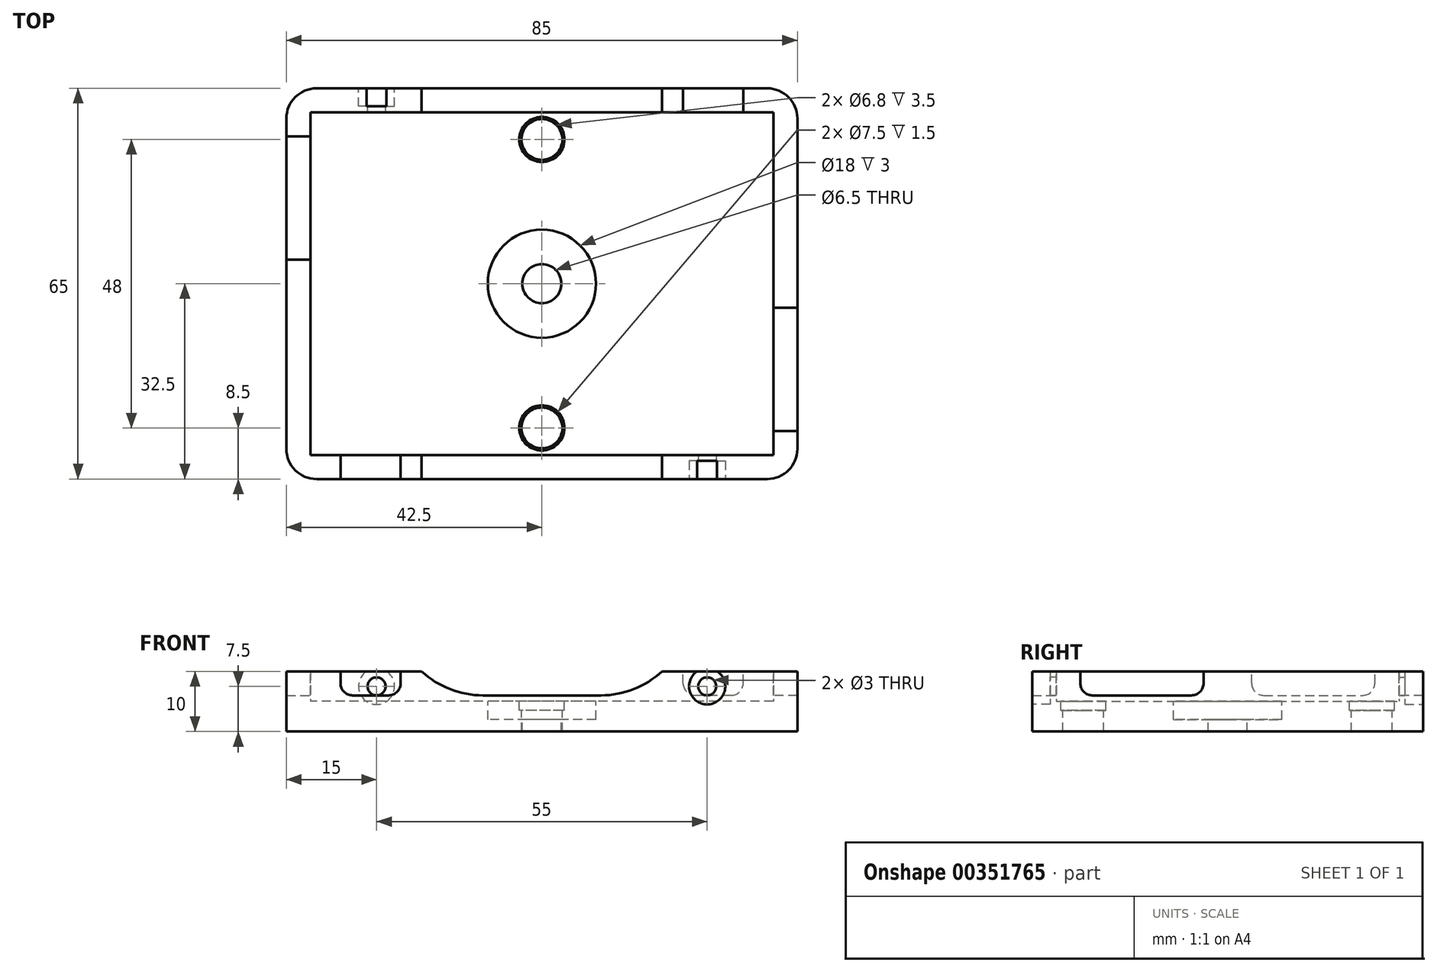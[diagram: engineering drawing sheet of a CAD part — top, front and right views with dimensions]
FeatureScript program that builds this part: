
annotation { "Feature Type Name" : "Feature", "Feature Type Description" : "" }
export const myFeature = defineFeature(function(context is Context, id is Id, definition is map)
    precondition{}
    {
        {
            var Q0;
            Q0=qCreatedBy(makeId("Top.planeOp"),FACE);
            var sketch = newSketch(context, id + "F0", { "sketchPlane" : qUnion([Q0])});
            skLineSegment(sketch, "E0.bottom", {"start": v(38.5, -28.5) * mm, "end": v(-38.5, -28.5) * mm});
            skLineSegment(sketch, "E0.top", {"start": v(38.5, 28.5) * mm, "end": v(-38.5, 28.5) * mm});
            skLineSegment(sketch, "E0.left", {"start": v(38.5, -28.5) * mm, "end": v(38.5, 28.5) * mm});
            skLineSegment(sketch, "E0.right", {"start": v(-38.5, -28.5) * mm, "end": v(-38.5, 28.5) * mm});
            skPoint(sketch, "E0.middle", {"position": v(0, 0) * mm});
            skLineSegment(sketch, "E1.0", {"start": v(42.5, 32.5) * mm, "end": v(-42.5, 32.5) * mm});
            skLineSegment(sketch, "E1.1", {"start": v(42.5, -32.5) * mm, "end": v(42.5, 32.5) * mm});
            skLineSegment(sketch, "E1.2", {"start": v(42.5, -32.5) * mm, "end": v(-42.5, -32.5) * mm});
            skLineSegment(sketch, "E1.3", {"start": v(-42.5, -32.5) * mm, "end": v(-42.5, 32.5) * mm});
            skSolve(sketch);
        }
        {
            var Q0;
            Q0=makeQuery(id+"F0.imprint","IMPRINT",FACE,{"disambiguationData":[TD([[makeQuery(id+"F0.imprint","IMPRINT",EDGE,{"derivedFrom":sQuery(id+"F0.wireOp",EDGE,"E0.bottom")}),-1.0]])]});
            var Q1;
            Q1=makeQuery(id+"F0.imprint","IMPRINT",FACE,{"disambiguationData":[TD([[makeQuery(id+"F0.imprint","IMPRINT",EDGE,{"derivedFrom":sQuery(id+"F0.wireOp",EDGE,"E0.bottom")}),1.0]])]});
            extrude(context, id + "F1", {"entities" : qUnion([Q0, Q1]), "oppositeDirection" : true, "depth" : 5 * mm, "offsetDistance" : 25 * mm});
        }
        {
            var Q0;
            Q0=makeQuery(id+"F0.imprint","IMPRINT",FACE,{"disambiguationData":[TD([[makeQuery(id+"F0.imprint","IMPRINT",EDGE,{"derivedFrom":sQuery(id+"F0.wireOp",EDGE,"E0.bottom")}),1.0]])]});
            extrude(context, id + "F2", {"entities" : qUnion([Q0]), "operationType" : NewBodyOperationType.ADD, "depth" : 5 * mm, "offsetDistance" : 25 * mm});
        }
        {
            var Q0;
            Q0=makeQuery(id+"F2.opExtrude","CAP_FACE",FACE,{"disambiguationData":[OSD([sQuery(id+"F0.wireOp",EDGE,"E0.bottom"),sQuery(id+"F0.wireOp",EDGE,"E0.top"),sQuery(id+"F0.wireOp",EDGE,"E0.left"),sQuery(id+"F0.wireOp",EDGE,"E0.right"),sQuery(id+"F0.wireOp",EDGE,"E1.0"),sQuery(id+"F0.wireOp",EDGE,"E1.1"),sQuery(id+"F0.wireOp",EDGE,"E1.2"),sQuery(id+"F0.wireOp",EDGE,"E1.3")])],"isStart":false});
            var sketch = newSketch(context, id + "F3", { "sketchPlane" : qUnion([Q0])});
            skLineSegment(sketch, "E2.bottom", {"start": v(20, 28.5) * mm, "end": v(-20, 28.5) * mm});
            skLineSegment(sketch, "E2.top", {"start": v(20, 32.5) * mm, "end": v(-20, 32.5) * mm});
            skLineSegment(sketch, "E2.left", {"start": v(20, 28.5) * mm, "end": v(20, 32.5) * mm});
            skLineSegment(sketch, "E2.right", {"start": v(-20, 28.5) * mm, "end": v(-20, 32.5) * mm});
            skPoint(sketch, "E2.middle", {"position": v(0, 30.5) * mm});
            skPoint(sketch, "E2.middle.positionSnap0", {"position": v(0, 32.5) * mm});
            skPoint(sketch, "E2.centerSnap0", {"position": v(0, 32.5) * mm});
            skLineSegment(sketch, "E3.bottom", {"start": v(20, -32.5) * mm, "end": v(-20, -32.5) * mm});
            skLineSegment(sketch, "E3.top", {"start": v(20, -28.5) * mm, "end": v(-20, -28.5) * mm});
            skLineSegment(sketch, "E3.left", {"start": v(20, -32.5) * mm, "end": v(20, -28.5) * mm});
            skLineSegment(sketch, "E3.right", {"start": v(-20, -32.5) * mm, "end": v(-20, -28.5) * mm});
            skPoint(sketch, "E3.middle", {"position": v(0, -30.5) * mm});
            skPoint(sketch, "E3.middle.positionSnap0", {"position": v(0, -32.5) * mm});
            skPoint(sketch, "E3.centerSnap0", {"position": v(0, -32.5) * mm});
            skLineSegment(sketch, "E4.bottom", {"start": v(-23.5, -28.5) * mm, "end": v(-33.5, -28.5) * mm});
            skLineSegment(sketch, "E4.top", {"start": v(-23.5, -32.5) * mm, "end": v(-33.5, -32.5) * mm});
            skLineSegment(sketch, "E4.left", {"start": v(-23.5, -28.5) * mm, "end": v(-23.5, -32.5) * mm});
            skLineSegment(sketch, "E4.right", {"start": v(-33.5, -28.5) * mm, "end": v(-33.5, -32.5) * mm});
            skPoint(sketch, "E4.middle", {"position": v(-28.5, -30.5) * mm});
            skLineSegment(sketch, "E5.bottom", {"start": v(33.5, 32.5) * mm, "end": v(23.5, 32.5) * mm});
            skLineSegment(sketch, "E5.top", {"start": v(33.5, 28.5) * mm, "end": v(23.5, 28.5) * mm});
            skLineSegment(sketch, "E5.left", {"start": v(33.5, 32.5) * mm, "end": v(33.5, 28.5) * mm});
            skLineSegment(sketch, "E5.right", {"start": v(23.5, 32.5) * mm, "end": v(23.5, 28.5) * mm});
            skPoint(sketch, "E5.middle", {"position": v(28.5, 30.5) * mm});
            skLineSegment(sketch, "E6.bottom", {"start": v(-42.5, 24.5) * mm, "end": v(-38.5, 24.5) * mm});
            skLineSegment(sketch, "E6.top", {"start": v(-42.5, 4) * mm, "end": v(-38.5, 4) * mm});
            skLineSegment(sketch, "E6.left", {"start": v(-42.5, 24.5) * mm, "end": v(-42.5, 4) * mm});
            skLineSegment(sketch, "E6.right", {"start": v(-38.5, 24.5) * mm, "end": v(-38.5, 4) * mm});
            skLineSegment(sketch, "E7.bottom", {"start": v(42.5, -24.5) * mm, "end": v(38.5, -24.5) * mm});
            skLineSegment(sketch, "E7.top", {"start": v(42.5, -4) * mm, "end": v(38.5, -4) * mm});
            skLineSegment(sketch, "E7.left", {"start": v(42.5, -24.5) * mm, "end": v(42.5, -4) * mm});
            skLineSegment(sketch, "E7.right", {"start": v(38.5, -24.5) * mm, "end": v(38.5, -4) * mm});
            skSolve(sketch);
        }
        {
            var Q0;
            Q0=makeQuery(id+"F3.imprint","IMPRINT",FACE,{"disambiguationData":[TD([[makeQuery(id+"F3.imprint","IMPRINT",EDGE,{"derivedFrom":sQuery(id+"F3.wireOp",EDGE,"E5.bottom")}),1.0]])]});
            var Q1;
            Q1=makeQuery(id+"F3.imprint","IMPRINT",FACE,{"disambiguationData":[TD([[makeQuery(id+"F3.imprint","IMPRINT",EDGE,{"derivedFrom":sQuery(id+"F3.wireOp",EDGE,"E2.bottom")}),-1.0]])]});
            var Q2;
            Q2=makeQuery(id+"F3.imprint","IMPRINT",FACE,{"disambiguationData":[TD([[makeQuery(id+"F3.imprint","IMPRINT",EDGE,{"derivedFrom":sQuery(id+"F3.wireOp",EDGE,"E3.bottom")}),-1.0]])]});
            var Q3;
            Q3=makeQuery(id+"F3.imprint","IMPRINT",FACE,{"disambiguationData":[TD([[makeQuery(id+"F3.imprint","IMPRINT",EDGE,{"derivedFrom":sQuery(id+"F3.wireOp",EDGE,"E4.bottom")}),1.0]])]});
            var Q4;
            Q4=makeQuery(id+"F3.imprint","IMPRINT",FACE,{"disambiguationData":[TD([[makeQuery(id+"F3.imprint","IMPRINT",EDGE,{"derivedFrom":sQuery(id+"F3.wireOp",EDGE,"E6.bottom")}),-1.0]])]});
            var Q5;
            Q5=makeQuery(id+"F3.imprint","IMPRINT",FACE,{"disambiguationData":[TD([[makeQuery(id+"F3.imprint","IMPRINT",EDGE,{"derivedFrom":sQuery(id+"F3.wireOp",EDGE,"E7.bottom")}),-1.0]])]});
            extrude(context, id + "F4", {"entities" : qUnion([Q0, Q1, Q2, Q3, Q4, Q5]), "operationType" : NewBodyOperationType.REMOVE, "oppositeDirection" : true, "depth" : 4 * mm, "offsetDistance" : 25 * mm});
        }
        {
            var Q0;
            Q0=makeQuery(id+"F4.boolean.opBoolean","COPY",EDGE,{"derivedFrom":makeQuery(id+"F4.opExtrude","CAP_EDGE",EDGE,{"disambiguationData":[OSD([sQuery(id+"F3.wireOp",EDGE,"E2.right")])],"isStart":false})});
            var Q1;
            Q1=makeQuery(id+"F4.boolean.opBoolean","COPY",EDGE,{"derivedFrom":makeQuery(id+"F4.opExtrude","CAP_EDGE",EDGE,{"disambiguationData":[OSD([sQuery(id+"F3.wireOp",EDGE,"E2.left")])],"isStart":false})});
            var Q2;
            Q2=makeQuery(id+"F4.boolean.opBoolean","COPY",EDGE,{"derivedFrom":makeQuery(id+"F4.opExtrude","CAP_EDGE",EDGE,{"disambiguationData":[OSD([sQuery(id+"F3.wireOp",EDGE,"E3.left")])],"isStart":false})});
            var Q3;
            Q3=makeQuery(id+"F4.boolean.opBoolean","COPY",EDGE,{"derivedFrom":makeQuery(id+"F4.opExtrude","CAP_EDGE",EDGE,{"disambiguationData":[OSD([sQuery(id+"F3.wireOp",EDGE,"E3.right")])],"isStart":false})});
            fillet(context, id + "F5", {"entities" : qUnion([Q0, Q1, Q2, Q3]), "radius" : 15 * mm, "tangentPropagation" : true, "allowEdgeOverflow" : false});
        }
        {
            var Q0;
            Q0=makeQuery(id+"F4.boolean.opBoolean","COPY",EDGE,{"derivedFrom":makeQuery(id+"F4.opExtrude","CAP_EDGE",EDGE,{"disambiguationData":[OSD([sQuery(id+"F3.wireOp",EDGE,"E7.top")])],"isStart":false})});
            var Q1;
            Q1=makeQuery(id+"F4.boolean.opBoolean","COPY",EDGE,{"derivedFrom":makeQuery(id+"F4.opExtrude","CAP_EDGE",EDGE,{"disambiguationData":[OSD([sQuery(id+"F3.wireOp",EDGE,"E7.bottom")])],"isStart":false})});
            var Q2;
            Q2=makeQuery(id+"F4.boolean.opBoolean","COPY",EDGE,{"derivedFrom":makeQuery(id+"F4.opExtrude","CAP_EDGE",EDGE,{"disambiguationData":[OSD([sQuery(id+"F3.wireOp",EDGE,"E6.bottom")])],"isStart":false})});
            var Q3;
            Q3=makeQuery(id+"F4.boolean.opBoolean","COPY",EDGE,{"derivedFrom":makeQuery(id+"F4.opExtrude","CAP_EDGE",EDGE,{"disambiguationData":[OSD([sQuery(id+"F3.wireOp",EDGE,"E6.top")])],"isStart":false})});
            var Q4;
            Q4=makeQuery(id+"F4.boolean.opBoolean","COPY",EDGE,{"derivedFrom":makeQuery(id+"F4.opExtrude","CAP_EDGE",EDGE,{"disambiguationData":[OSD([sQuery(id+"F3.wireOp",EDGE,"E4.right")])],"isStart":false})});
            var Q5;
            Q5=makeQuery(id+"F4.boolean.opBoolean","COPY",EDGE,{"derivedFrom":makeQuery(id+"F4.opExtrude","CAP_EDGE",EDGE,{"disambiguationData":[OSD([sQuery(id+"F3.wireOp",EDGE,"E4.left")])],"isStart":false})});
            var Q6;
            Q6=makeQuery(id+"F4.boolean.opBoolean","COPY",EDGE,{"derivedFrom":makeQuery(id+"F4.opExtrude","CAP_EDGE",EDGE,{"disambiguationData":[OSD([sQuery(id+"F3.wireOp",EDGE,"E5.left")])],"isStart":false})});
            var Q7;
            Q7=makeQuery(id+"F4.boolean.opBoolean","COPY",EDGE,{"derivedFrom":makeQuery(id+"F4.opExtrude","CAP_EDGE",EDGE,{"disambiguationData":[OSD([sQuery(id+"F3.wireOp",EDGE,"E5.right")])],"isStart":false})});
            fillet(context, id + "F6", {"entities" : qUnion([Q0, Q1, Q2, Q3, Q4, Q5, Q6, Q7]), "radius" : 2 * mm, "tangentPropagation" : true, "allowEdgeOverflow" : false});
        }
        {
            var Q0;
            Q0=makeQuery(id+"F0.imprint","IMPRINT",FACE,{"disambiguationData":[TD([[makeQuery(id+"F0.imprint","IMPRINT",EDGE,{"derivedFrom":sQuery(id+"F0.wireOp",EDGE,"E0.bottom")}),-1.0]])]});
            var sketch = newSketch(context, id + "F7", { "sketchPlane" : qUnion([Q0])});
            skCircle(sketch, "E8", {"center": v(0, 24) * mm, "radius": 3.25 * mm});
            skCircle(sketch, "E9", {"center": v(0, -24) * mm, "radius": 3.25 * mm});
            skSolve(sketch);
        }
        {
            var Q0;
            Q0=sQuery(id+"F7.wireOp",VERTEX,"E8.center");
            var Q1;
            Q1=sQuery(id+"F7.wireOp",VERTEX,"E9.center");
            var Q2;
            Q2=makeQuery(id+"F1.opExtrude","SWEPT_BODY",BODY,{"disambiguationData":[OSD([sQuery(id+"F0.wireOp",EDGE,"E1.0"),sQuery(id+"F0.wireOp",EDGE,"E1.1"),sQuery(id+"F0.wireOp",EDGE,"E1.2"),sQuery(id+"F0.wireOp",EDGE,"E1.3")])]});
            hole(context, id + "F8", {"style" : HoleStyle.C_BORE, "endStyle" : HoleEndStyle.THROUGH, "holeDiameter" : 6.8 * mm, "cBoreDiameter" : 7.5 * mm, "cBoreDepth" : 1.5 * mm, "majorDiameter" : 5 * mm, "isTappedThrough" : true, "tappedDepth" : 12 * mm, "tapClearance" : 3, "locations" : qUnion([Q0, Q1]), "scope" : qUnion([Q2])});
        }
        {
            var Q0;
            Q0=makeQuery(id+"F0.imprint","IMPRINT",FACE,{"disambiguationData":[TD([[makeQuery(id+"F0.imprint","IMPRINT",EDGE,{"derivedFrom":sQuery(id+"F0.wireOp",EDGE,"E0.bottom")}),-1.0]])]});
            var sketch = newSketch(context, id + "F9", { "sketchPlane" : qUnion([Q0])});
            skCircle(sketch, "E10", {"center": v(0, 0) * mm, "radius": 9 * mm});
            skCircle(sketch, "E11", {"center": v(0, 0) * mm, "radius": 3.25 * mm});
            skSolve(sketch);
        }
        {
            var Q0;
            Q0 = qSketchRegion(id + "F9", true);
            extrude(context, id + "F10", {"entities" : qUnion([Q0]), "operationType" : NewBodyOperationType.REMOVE, "oppositeDirection" : true, "depth" : 3 * mm, "offsetDistance" : 25 * mm});
        }
        {
            var Q0;
            Q0=makeQuery(id+"F9.imprint","IMPRINT",FACE,{"disambiguationData":[TD([[makeQuery(id+"F9.imprint","IMPRINT",EDGE,{"derivedFrom":sQuery(id+"F9.wireOp",EDGE,"E11")}),1.0]])]});
            extrude(context, id + "F11", {"entities" : qUnion([Q0]), "operationType" : NewBodyOperationType.REMOVE, "oppositeDirection" : true, "depth" : 25 * mm, "offsetDistance" : 25 * mm});
        }
        {
            var Q0;
            {var subQ0=sQuery(id+"F0.wireOp",EDGE,"E1.2");var subQ1=sQuery(id+"F0.wireOp",EDGE,"E1.1");Q0=makeQuery(id+"F2.boolean.opBoolean","MERGE",EDGE,{"derivedFrom":[makeQuery(id+"F1.opExtrude","SWEPT_EDGE",EDGE,{"disambiguationData":[OSD([subQ1,subQ0])]}),makeQuery(id+"F2.opExtrude","SWEPT_EDGE",EDGE,{"disambiguationData":[OSD([subQ1,subQ0])]})]});}
            var Q1;
            {var subQ0=sQuery(id+"F0.wireOp",EDGE,"E1.1");var subQ1=sQuery(id+"F0.wireOp",EDGE,"E1.0");Q1=makeQuery(id+"F2.boolean.opBoolean","MERGE",EDGE,{"derivedFrom":[makeQuery(id+"F1.opExtrude","SWEPT_EDGE",EDGE,{"disambiguationData":[OSD([subQ1,subQ0])]}),makeQuery(id+"F2.opExtrude","SWEPT_EDGE",EDGE,{"disambiguationData":[OSD([subQ1,subQ0])]})]});}
            var Q2;
            {var subQ0=sQuery(id+"F0.wireOp",EDGE,"E1.3");var subQ1=sQuery(id+"F0.wireOp",EDGE,"E1.2");Q2=makeQuery(id+"F2.boolean.opBoolean","MERGE",EDGE,{"derivedFrom":[makeQuery(id+"F1.opExtrude","SWEPT_EDGE",EDGE,{"disambiguationData":[OSD([subQ1,subQ0])]}),makeQuery(id+"F2.opExtrude","SWEPT_EDGE",EDGE,{"disambiguationData":[OSD([subQ1,subQ0])]})]});}
            var Q3;
            {var subQ0=sQuery(id+"F0.wireOp",EDGE,"E1.3");var subQ1=sQuery(id+"F0.wireOp",EDGE,"E1.0");Q3=makeQuery(id+"F2.boolean.opBoolean","MERGE",EDGE,{"derivedFrom":[makeQuery(id+"F1.opExtrude","SWEPT_EDGE",EDGE,{"disambiguationData":[OSD([subQ1,subQ0])]}),makeQuery(id+"F2.opExtrude","SWEPT_EDGE",EDGE,{"disambiguationData":[OSD([subQ1,subQ0])]})]});}
            fillet(context, id + "F12", {"entities" : qUnion([Q0, Q1, Q2, Q3]), "radius" : 5 * mm, "tangentPropagation" : true, "allowEdgeOverflow" : false});
        }
        {
            var Q0;
            {var subQ0=sQuery(id+"F0.wireOp",EDGE,"E1.2");Q0=makeQuery(id+"F2.boolean.opBoolean","MERGE",FACE,{"derivedFrom":[makeQuery(id+"F1.opExtrude","SWEPT_FACE",FACE,{"disambiguationData":[OSD([subQ0])]}),makeQuery(id+"F2.opExtrude","SWEPT_FACE",FACE,{"disambiguationData":[OSD([subQ0])]})]});}
            var sketch = newSketch(context, id + "F13", { "sketchPlane" : qUnion([Q0])});
            skCircle(sketch, "E12", {"center": v(27.5, 2.5) * mm, "radius": 1.5 * mm});
            skSolve(sketch);
        }
        {
            var Q0;
            {var subQ0=sQuery(id+"F0.wireOp",EDGE,"E1.0");Q0=makeQuery(id+"F2.boolean.opBoolean","MERGE",FACE,{"derivedFrom":[makeQuery(id+"F1.opExtrude","SWEPT_FACE",FACE,{"disambiguationData":[OSD([subQ0])]}),makeQuery(id+"F2.opExtrude","SWEPT_FACE",FACE,{"disambiguationData":[OSD([subQ0])]})]});}
            var sketch = newSketch(context, id + "F14", { "sketchPlane" : qUnion([Q0])});
            skCircle(sketch, "E13", {"center": v(27.5, 2.5) * mm, "radius": 3.38 * mm});
            skSolve(sketch);
        }
        {
            var Q0;
            Q0=sQuery(id+"F14.wireOp",VERTEX,"E13.center");
            var Q1;
            Q1=sQuery(id+"F13.wireOp",VERTEX,"E12.center");
            var Q2;
            Q2=makeQuery(id+"F1.opExtrude","SWEPT_BODY",BODY,{"disambiguationData":[OSD([sQuery(id+"F0.wireOp",EDGE,"E1.0"),sQuery(id+"F0.wireOp",EDGE,"E1.1"),sQuery(id+"F0.wireOp",EDGE,"E1.2"),sQuery(id+"F0.wireOp",EDGE,"E1.3")])]});
            hole(context, id + "F15", {"style" : HoleStyle.C_BORE, "endStyle" : HoleEndStyle.THROUGH, "holeDiameter" : 3 * mm, "cBoreDiameter" : 6 * mm, "cBoreDepth" : 3 * mm, "majorDiameter" : 5 * mm, "isTappedThrough" : true, "tappedDepth" : 12 * mm, "tapClearance" : 3, "locations" : qUnion([Q0, Q1]), "scope" : qUnion([Q2])});
        }
    });
